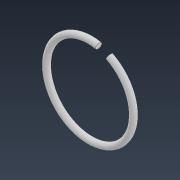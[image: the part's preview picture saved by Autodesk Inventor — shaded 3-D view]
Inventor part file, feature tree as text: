
AUTODESK INVENTOR PART (.ipt)
format: ipt  version: 2022 (Build 260153000, 153)  size: 112,640 bytes
history: native  units: mm
features: sketch x2, plane x1, sweep x1
ambient origin geometry x8: Origin, YZ Plane, XZ Plane, XY Plane, X Axis, Y Axis, Z Axis, Center Point
bodies: Solid1 (feature_tree)
feature tree (4):
  sketch  "Sketch1"  dims[d0=15.0deg d1=42.0mm]
  plane  "Work Plane1"
  sweep  "Sweep1"
  sketch  "Sketch2"  dims[d2=3.0mm d3=0.0mm d4=0.0mm]
